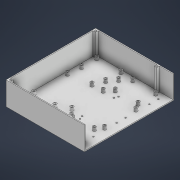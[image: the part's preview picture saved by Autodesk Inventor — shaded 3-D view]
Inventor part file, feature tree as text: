
AUTODESK INVENTOR PART (.ipt)
format: ipt  version: 2021 (Build 250183000, 183)  size: 374,272 bytes
history: native  units: mm
features: extrude x7, sketch x7, projected_geometry x6
ambient origin geometry x8: Origin, YZ Plane, XZ Plane, XY Plane, X Axis, Y Axis, Z Axis, Center Point
bodies: Volumenkörper1 (feature_tree)
feature tree (20):
  extrude  "Extrusion1"  Depth=200.0mm
  extrude  "Extrusion2"  Depth=2.0mm
  extrude  "Extrusion4"  Depth=17.5mm
  extrude  "Extrusion5"  Depth=20.0mm
  extrude  "Extrusion6"  Depth=2.0mm TaperAngle=0.0deg
  extrude  "Extrusion7"  Depth=2.0mm
  extrude  "Extrusion8"  Depth=6.0mm
  sketch  "Skizze1"  dims[d0=175.0mm d1=200.0mm]
  sketch  "Skizze2"  dims[d2=2.0mm d3=0.0mm d4=3.2mm]
  sketch  "Skizze4"  dims[d5=17.5mm d6=17.5mm]
  sketch  "Skizze5"  dims[d7=3.2mm d8=20.0mm]
  sketch  "Skizze6"  dims[d9=17.5mm d10=2.0mm d11=0.0mm]
  sketch  "Skizze7"  dims[d18=2.0mm d19=2.0mm]
  sketch  "Skizze8"  dims[d21=6.0mm d23=6.0mm d24=2.0mm d25=6.0mm d26=6.0mm d27=6.0mm d28=6.0mm d29=50.0mm d30=0.0mm d31=7.0mm d32=7.0mm d35=20.0mm d36=20.0mm d37=7.0mm d38=73.0mm d40=7.0mm d42=73.0mm d43=7.0mm d44=0.0mm d45=4.0mm d46=4.0mm d47=4.0mm d48=0.0mm d49=4.0mm d50=73.0mm d51=70.0mm d52=5.0mm d53=0.0mm d54=4.0mm d55=4.0mm d56=4.0mm d57=4.0mm d59=3.0mm d61=3.0mm d62=3.0mm d63=3.0mm d64=3.0mm d65=3.0mm d66=5.0mm d67=0.0mm d68=70.0mm d69=70.0mm d70=35.0mm d73=65.0mm d74=7.0mm d75=7.0mm d83=7.0mm d86=7.0mm d96=4.0mm d97=0.0mm d98=0.0mm d99=4.0mm d100=0.0mm d101=0.0mm d102=4.0mm d103=0.0mm d104=4.0mm d105=0.0mm d119=3.2mm d120=18.0mm d121=10.0mm d122=3.2mm d123=3.2mm d124=66.891mm d125=69.627mm d126=42.961mm d127=35.444mm d128=10.0mm d129=0.0mm d130=6.0mm d131=30.0mm d132=6.0mm d133=30.0mm d136=48.26mm d137=74.93mm d138=48.26mm d139=82.55mm d142=30.0mm d143=30.0mm d144=34.225mm d145=47.055mm d146=3.0mm d147=3.0mm d148=7.0mm d149=7.0mm d150=7.0mm d151=7.0mm d152=10.0mm d153=10.0mm d154=39.0mm d155=39.0mm d156=51.0mm d157=51.0mm d161=7.5mm d163=7.5mm d164=7.0mm d165=0.0mm d166=0.0mm d167=4.0mm d168=7.0mm d169=0.0mm d170=4.0mm d171=4.0mm d172=0.0mm d173=7.0mm d174=7.0mm d176=4.0mm d177=7.0mm d178=7.0mm d179=7.0mm d180=7.0mm d181=10.0mm d182=10.0mm d183=7.5mm d184=34.0mm d185=7.5mm d186=34.0mm d187=54.0mm d188=54.0mm d189=4.0mm d190=4.0mm d191=4.0mm d192=4.0mm d193=7.0mm d194=25.0mm d195=9.0mm d196=7.0mm d197=25.0mm d198=9.0mm d199=4.0mm d200=4.0mm]
  projected_geometry  "Projizierte Kontur1"
  projected_geometry  "Projizierte Kontur2"
  projected_geometry  "Projizierte Kontur3"
  projected_geometry  "Projizierte Kontur4"
  projected_geometry  "Projizierte Kontur5"
  projected_geometry  "Projizierte Kontur6"
